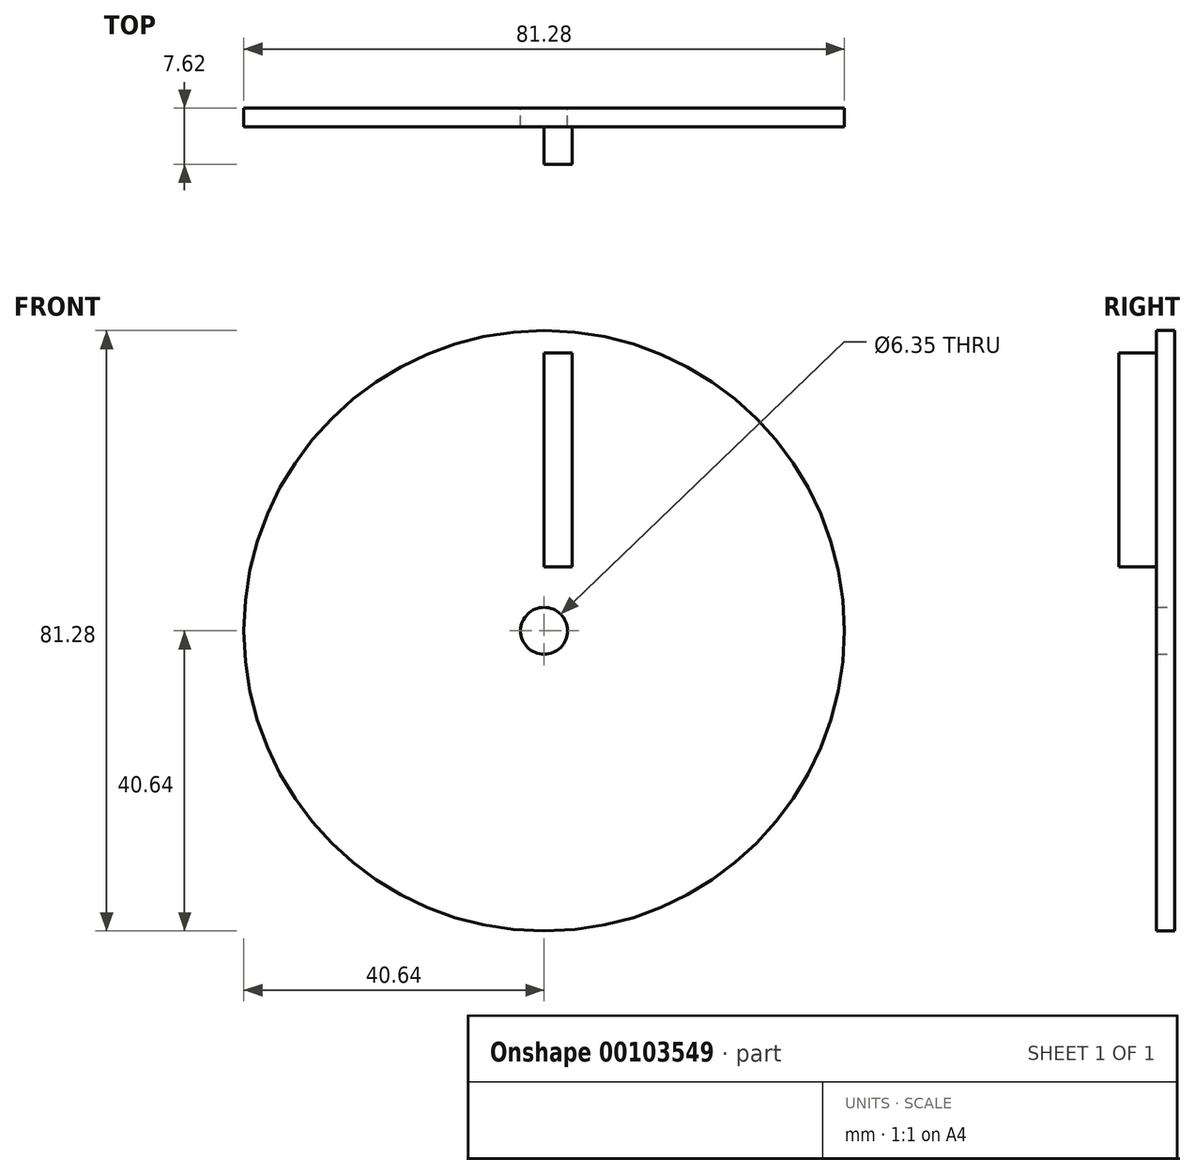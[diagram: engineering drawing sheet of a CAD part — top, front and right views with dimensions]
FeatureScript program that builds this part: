
annotation { "Feature Type Name" : "Feature", "Feature Type Description" : "" }
export const myFeature = defineFeature(function(context is Context, id is Id, definition is map)
    precondition{}
    {
        {
            var Q0;
            Q0=qCreatedBy(makeId("Front.planeOp"),FACE);
            var sketch = newSketch(context, id + "F0", { "sketchPlane" : qUnion([Q0])});
            skCircle(sketch, "E0", {"center": v(0, 0) * mm, "radius": 40.64 * mm});
            skCircle(sketch, "E1", {"center": v(0, 0) * mm, "radius": 3.18 * mm});
            skLineSegment(sketch, "E2", {"start": v(0, 3.18) * mm, "end": v(0, 37.6) * mm});
            skLineSegment(sketch, "E3", {"start": v(0, 37.6) * mm, "end": v(3.77, 37.6) * mm});
            skLineSegment(sketch, "E4", {"start": v(3.77, 37.6) * mm, "end": v(3.77, 8.65) * mm});
            skLineSegment(sketch, "E5", {"start": v(3.77, 8.65) * mm, "end": v(0, 8.65) * mm});
            skSolve(sketch);
        }
        {
            var Q0;
            Q0=makeQuery(id+"F0.imprint","IMPRINT",FACE,{"disambiguationData":[TD([[makeQuery(id+"F0.imprint","IMPRINT",EDGE,{"derivedFrom":sQuery(id+"F0.wireOp",EDGE,"E0")}),1.0]])]});
            extrude(context, id + "F1", {"entities" : qUnion([Q0]), "depth" : 2.54 * mm});
        }
        {
            var Q0;
            {var subQ0=sQuery(id+"F0.wireOp",EDGE,"E3");Q0=makeQuery(id+"F0.imprint","IMPRINT",FACE,{"disambiguationData":[TD([[makeQuery(id+"F0.imprint","IMPRINT",EDGE,{"derivedFrom":subQ0}),-1.0]])]});}
            extrude(context, id + "F2", {"entities" : qUnion([Q0]), "operationType" : NewBodyOperationType.ADD, "depth" : 7.62 * mm});
        }
    });
